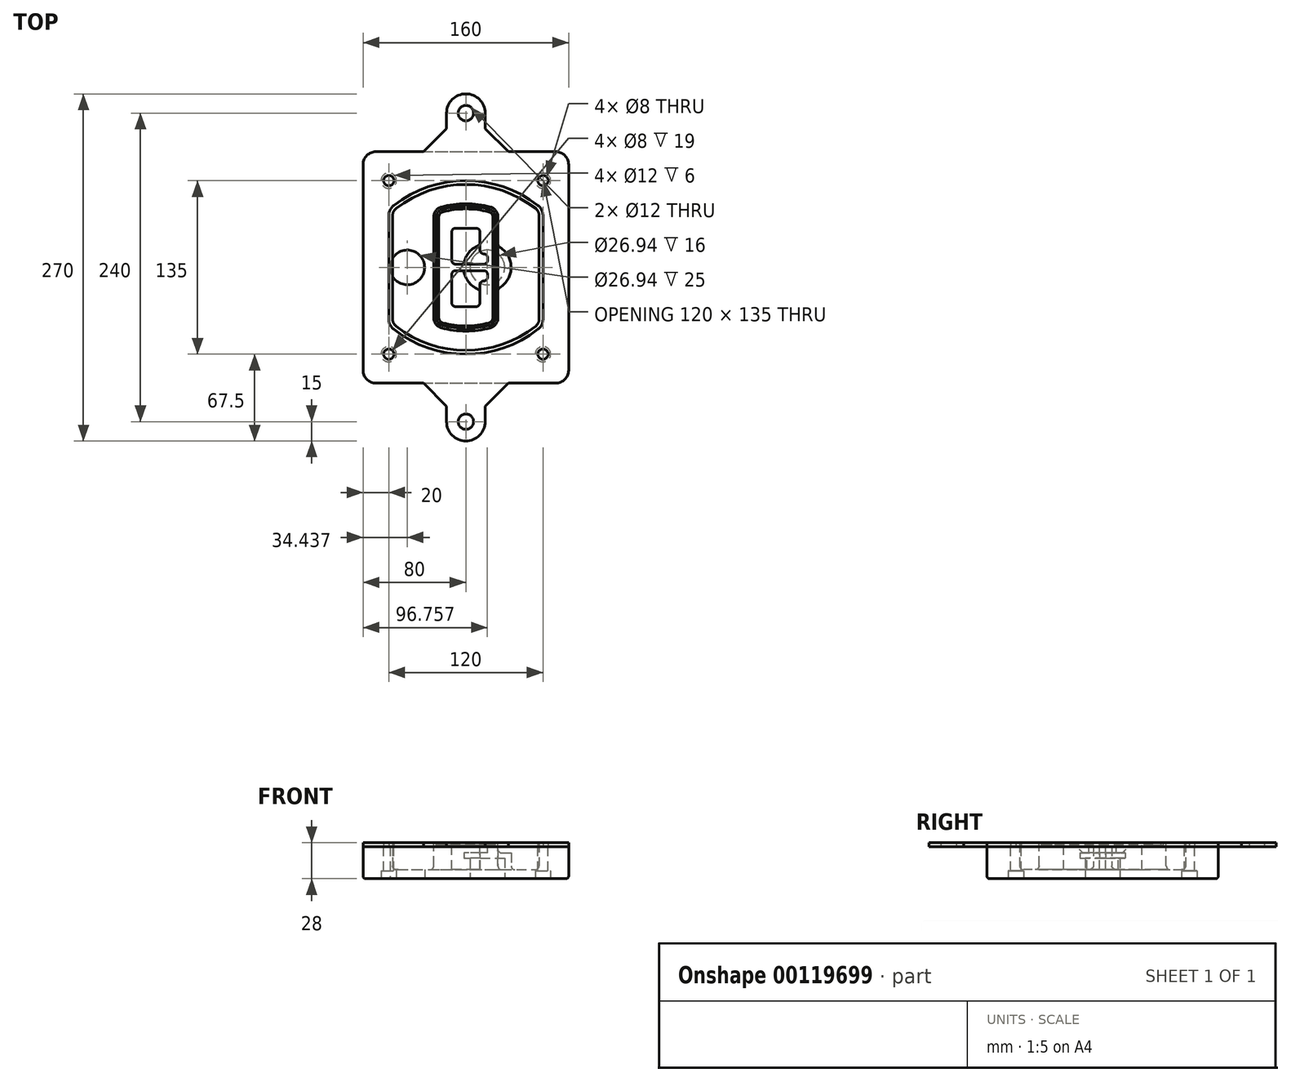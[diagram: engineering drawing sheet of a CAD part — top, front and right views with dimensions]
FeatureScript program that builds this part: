
annotation { "Feature Type Name" : "Feature", "Feature Type Description" : "" }
export const myFeature = defineFeature(function(context is Context, id is Id, definition is map)
    precondition{}
    {
        {
            var Q0;
            Q0=qCreatedBy(makeId("Top.planeOp"),FACE);
            var sketch = newSketch(context, id + "F0", { "sketchPlane" : qUnion([Q0])});
            skPoint(sketch, "E0.rect.middle", {"position": v(0, 0) * mm});
            skLineSegment(sketch, "E1.bottom", {"start": v(-70, -90) * mm, "end": v(70, -90) * mm});
            skLineSegment(sketch, "E1.top", {"start": v(-70, 90) * mm, "end": v(70, 90) * mm});
            skLineSegment(sketch, "E1.left", {"start": v(-80, -80) * mm, "end": v(-80, 80) * mm});
            skLineSegment(sketch, "E1.right", {"start": v(80, -80) * mm, "end": v(80, 80) * mm});
            skLineSegment(sketch, "E2", {"start": v(-80, 90) * mm, "end": v(80, -90) * mm, "construction": true});
            skLineSegment(sketch, "E3", {"start": v(80, 90) * mm, "end": v(-80, -90) * mm, "construction": true});
            skCircle(sketch, "E4", {"center": v(-60, 67.5) * mm, "radius": 4 * mm});
            skCircle(sketch, "E5", {"center": v(60, 67.5) * mm, "radius": 4 * mm});
            skCircle(sketch, "E6", {"center": v(60, -67.5) * mm, "radius": 4 * mm});
            skCircle(sketch, "E7", {"center": v(-60, -67.5) * mm, "radius": 4 * mm});
            skLineSegment(sketch, "E8", {"start": v(-60, 67.5) * mm, "end": v(60, 67.5) * mm, "construction": true});
            skLineSegment(sketch, "E9", {"start": v(60, 67.5) * mm, "end": v(60, -67.5) * mm, "construction": true});
            skLineSegment(sketch, "E10", {"start": v(60, -67.5) * mm, "end": v(-60, -67.5) * mm, "construction": true});
            skLineSegment(sketch, "E11", {"start": v(-60, -67.5) * mm, "end": v(-60, 67.5) * mm, "construction": true});
            skLineSegment(sketch, "E12", {"start": v(-60, 40.3) * mm, "end": v(-60, -40.3) * mm});
            skLineSegment(sketch, "E13", {"start": v(60, 40.3) * mm, "end": v(60, -40.3) * mm});
            skArc(sketch, "E14", {"start": v(56.15, 48.18) * mm, "mid": v(0, 67.5) * mm, "end": v(-56.15, 48.18) * mm});
            skArc(sketch, "E15", {"start": v(-56.15, -48.18) * mm, "mid": v(0, -67.5) * mm, "end": v(56.15, -48.18) * mm});
            skLineSegment(sketch, "E16", {"start": v(-60, 0) * mm, "end": v(60, 0) * mm, "construction": true});
            skPoint(sketch, "E17.visualSharp", {"position": v(-60, -45) * mm});
            skArc(sketch, "E17.filletArc", {"start": v(-60, -40.3) * mm, "mid": v(-58.99, -44.68) * mm, "end": v(-56.15, -48.18) * mm});
            skPoint(sketch, "E18.visualSharp", {"position": v(-60, 45) * mm});
            skArc(sketch, "E18.filletArc", {"start": v(-56.15, 48.18) * mm, "mid": v(-58.99, 44.68) * mm, "end": v(-60, 40.3) * mm});
            skPoint(sketch, "E19.visualSharp", {"position": v(60, 45) * mm});
            skArc(sketch, "E19.filletArc", {"start": v(60, 40.3) * mm, "mid": v(58.99, 44.68) * mm, "end": v(56.15, 48.18) * mm});
            skPoint(sketch, "E20.visualSharp", {"position": v(60, -45) * mm});
            skArc(sketch, "E20.filletArc", {"start": v(56.15, -48.18) * mm, "mid": v(58.99, -44.68) * mm, "end": v(60, -40.3) * mm});
            skPoint(sketch, "E21.visualSharp", {"position": v(-80, 90) * mm});
            skArc(sketch, "E21.filletArc", {"start": v(-70, 90) * mm, "mid": v(-77.07, 87.07) * mm, "end": v(-80, 80) * mm});
            skPoint(sketch, "E22.visualSharp", {"position": v(80, 90) * mm});
            skArc(sketch, "E22.filletArc", {"start": v(80, 80) * mm, "mid": v(77.07, 87.07) * mm, "end": v(70, 90) * mm});
            skPoint(sketch, "E23.visualSharp", {"position": v(80, -90) * mm});
            skArc(sketch, "E23.filletArc", {"start": v(70, -90) * mm, "mid": v(77.07, -87.07) * mm, "end": v(80, -80) * mm});
            skPoint(sketch, "E24.visualSharp", {"position": v(-80, -90) * mm});
            skArc(sketch, "E24.filletArc", {"start": v(-80, -80) * mm, "mid": v(-77.07, -87.07) * mm, "end": v(-70, -90) * mm});
            skArc(sketch, "E25.0", {"start": v(57, 40.3) * mm, "mid": v(56.3, 43.36) * mm, "end": v(54.3, 45.81) * mm});
            skLineSegment(sketch, "E25.1", {"start": v(57, 40.3) * mm, "end": v(57, -40.3) * mm});
            skArc(sketch, "E25.2", {"start": v(54.3, -45.81) * mm, "mid": v(56.3, -43.36) * mm, "end": v(57, -40.3) * mm});
            skArc(sketch, "E25.3", {"start": v(-54.3, -45.81) * mm, "mid": v(0, -64.5) * mm, "end": v(54.3, -45.81) * mm});
            skArc(sketch, "E25.4", {"start": v(-57, -40.3) * mm, "mid": v(-56.3, -43.36) * mm, "end": v(-54.3, -45.81) * mm});
            skArc(sketch, "E25.5", {"start": v(54.3, 45.81) * mm, "mid": v(0, 64.5) * mm, "end": v(-54.3, 45.81) * mm});
            skLineSegment(sketch, "E25.6", {"start": v(-57, 40.3) * mm, "end": v(-57, -40.3) * mm});
            skArc(sketch, "E25.7", {"start": v(-54.3, 45.81) * mm, "mid": v(-56.3, 43.36) * mm, "end": v(-57, 40.3) * mm});
            skArc(sketch, "E26.0", {"start": v(-58.62, 51.33) * mm, "mid": v(-62.58, 46.43) * mm, "end": v(-64, 40.3) * mm});
            skArc(sketch, "E26.1", {"start": v(58.62, 51.33) * mm, "mid": v(0, 71.5) * mm, "end": v(-58.62, 51.33) * mm});
            skArc(sketch, "E26.2", {"start": v(64, 40.3) * mm, "mid": v(62.58, 46.43) * mm, "end": v(58.62, 51.33) * mm});
            skLineSegment(sketch, "E26.3", {"start": v(64, 40.3) * mm, "end": v(64, -40.3) * mm});
            skArc(sketch, "E26.4", {"start": v(58.62, -51.33) * mm, "mid": v(62.58, -46.43) * mm, "end": v(64, -40.3) * mm});
            skLineSegment(sketch, "E26.5", {"start": v(-64, 40.3) * mm, "end": v(-64, -40.3) * mm});
            skArc(sketch, "E26.6", {"start": v(-58.62, -51.33) * mm, "mid": v(0, -71.5) * mm, "end": v(58.62, -51.33) * mm});
            skArc(sketch, "E26.7", {"start": v(-64, -40.3) * mm, "mid": v(-62.58, -46.43) * mm, "end": v(-58.62, -51.33) * mm});
            skSolve(sketch);
        }
        {
            var Q0;
            Q0=makeQuery(id+"F0.imprint","IMPRINT",FACE,{"disambiguationData":[TD([[makeQuery(id+"F0.imprint","IMPRINT",EDGE,{"derivedFrom":sQuery(id+"F0.wireOp",EDGE,"E1.bottom")}),1.0]])]});
            var Q1;
            Q1=makeQuery(id+"F0.imprint","IMPRINT",FACE,{"disambiguationData":[TD([[makeQuery(id+"F0.imprint","IMPRINT",EDGE,{"derivedFrom":sQuery(id+"F0.wireOp",EDGE,"E12")}),1.0]])]});
            var Q2;
            Q2=makeQuery(id+"F0.imprint","IMPRINT",FACE,{"disambiguationData":[TD([[makeQuery(id+"F0.imprint","IMPRINT",EDGE,{"derivedFrom":sQuery(id+"F0.wireOp",EDGE,"E25.0")}),1.0]])]});
            var Q3;
            Q3=makeQuery(id+"F0.imprint","IMPRINT",FACE,{"disambiguationData":[TD([[makeQuery(id+"F0.imprint","IMPRINT",EDGE,{"derivedFrom":sQuery(id+"F0.wireOp",EDGE,"E12")}),-1.0]])]});
            extrude(context, id + "F1", {"entities" : qUnion([Q0, Q1, Q2, Q3]), "oppositeDirection" : true, "depth" : 25 * mm});
        }
        {
            var Q0;
            Q0=makeQuery(id+"F0.imprint","IMPRINT",FACE,{"disambiguationData":[TD([[makeQuery(id+"F0.imprint","IMPRINT",EDGE,{"derivedFrom":sQuery(id+"F0.wireOp",EDGE,"E12")}),1.0]])]});
            extrude(context, id + "F2", {"entities" : qUnion([Q0]), "operationType" : NewBodyOperationType.ADD, "depth" : 3 * mm});
        }
        {
            var Q0;
            Q0=makeQuery(id+"F0.imprint","IMPRINT",FACE,{"disambiguationData":[TD([[makeQuery(id+"F0.imprint","IMPRINT",EDGE,{"derivedFrom":sQuery(id+"F0.wireOp",EDGE,"E25.0")}),1.0]])]});
            extrude(context, id + "F3", {"entities" : qUnion([Q0]), "operationType" : NewBodyOperationType.REMOVE, "oppositeDirection" : true, "depth" : 18 * mm});
        }
        {
            var Q0;
            Q0=makeQuery(id+"F2.opExtrude","CAP_FACE",FACE,{"disambiguationData":[OSD([sQuery(id+"F0.wireOp",EDGE,"E12"),sQuery(id+"F0.wireOp",EDGE,"E13"),sQuery(id+"F0.wireOp",EDGE,"E14"),sQuery(id+"F0.wireOp",EDGE,"E15"),sQuery(id+"F0.wireOp",EDGE,"E17.filletArc"),sQuery(id+"F0.wireOp",EDGE,"E18.filletArc"),sQuery(id+"F0.wireOp",EDGE,"E19.filletArc"),sQuery(id+"F0.wireOp",EDGE,"E20.filletArc"),sQuery(id+"F0.wireOp",EDGE,"E25.0"),sQuery(id+"F0.wireOp",EDGE,"E25.1"),sQuery(id+"F0.wireOp",EDGE,"E25.2"),sQuery(id+"F0.wireOp",EDGE,"E25.3"),sQuery(id+"F0.wireOp",EDGE,"E25.4"),sQuery(id+"F0.wireOp",EDGE,"E25.5"),sQuery(id+"F0.wireOp",EDGE,"E25.6"),sQuery(id+"F0.wireOp",EDGE,"E25.7")])],"isStart":false});
            var sketch = newSketch(context, id + "F4", { "sketchPlane" : qUnion([Q0])});
            skArc(sketch, "E27.0", {"start": v(-19.08, -46.97) * mm, "mid": v(0, -49.5) * mm, "end": v(19.08, -46.97) * mm});
            skArc(sketch, "E28.0", {"start": v(19.08, 46.97) * mm, "mid": v(0, 49.5) * mm, "end": v(-19.08, 46.97) * mm});
            skLineSegment(sketch, "E29", {"start": v(-25, 39.25) * mm, "end": v(-25, -39.25) * mm});
            skLineSegment(sketch, "E30", {"start": v(25, 39.25) * mm, "end": v(25, -39.25) * mm});
            skLineSegment(sketch, "E31", {"start": v(-25, 45.1) * mm, "end": v(25, 45.1) * mm, "construction": true});
            skLineSegment(sketch, "E32", {"start": v(-25, -45.1) * mm, "end": v(25, -45.1) * mm, "construction": true});
            skPoint(sketch, "E33.visualSharp", {"position": v(-25, 45.1) * mm});
            skArc(sketch, "E33.filletArc", {"start": v(-19.08, 46.97) * mm, "mid": v(-23.35, 44.11) * mm, "end": v(-25, 39.25) * mm});
            skPoint(sketch, "E34.visualSharp", {"position": v(25, 45.1) * mm});
            skArc(sketch, "E34.filletArc", {"start": v(25, 39.25) * mm, "mid": v(23.35, 44.11) * mm, "end": v(19.08, 46.97) * mm});
            skPoint(sketch, "E35.visualSharp", {"position": v(25, -45.1) * mm});
            skArc(sketch, "E35.filletArc", {"start": v(19.08, -46.97) * mm, "mid": v(23.35, -44.11) * mm, "end": v(25, -39.25) * mm});
            skPoint(sketch, "E36.visualSharp", {"position": v(-25, -45.1) * mm});
            skArc(sketch, "E36.filletArc", {"start": v(-25, -39.25) * mm, "mid": v(-23.35, -44.11) * mm, "end": v(-19.08, -46.97) * mm});
            skArc(sketch, "E37.0", {"start": v(54.3, 45.81) * mm, "mid": v(0, 64.5) * mm, "end": v(-54.3, 45.81) * mm});
            skArc(sketch, "E37.1", {"start": v(-54.3, 45.81) * mm, "mid": v(-56.3, 43.36) * mm, "end": v(-57, 40.3) * mm});
            skLineSegment(sketch, "E37.2", {"start": v(-57, 40.3) * mm, "end": v(-57, -40.3) * mm});
            skArc(sketch, "E37.3", {"start": v(-57, -40.3) * mm, "mid": v(-56.3, -43.36) * mm, "end": v(-54.3, -45.81) * mm});
            skArc(sketch, "E37.4", {"start": v(-54.3, -45.81) * mm, "mid": v(0, -64.5) * mm, "end": v(54.3, -45.81) * mm});
            skArc(sketch, "E37.5", {"start": v(54.3, -45.81) * mm, "mid": v(56.3, -43.36) * mm, "end": v(57, -40.3) * mm});
            skLineSegment(sketch, "E37.6", {"start": v(57, 40.3) * mm, "end": v(57, -40.3) * mm});
            skArc(sketch, "E37.7", {"start": v(57, 40.3) * mm, "mid": v(56.3, 43.36) * mm, "end": v(54.3, 45.81) * mm});
            skLineSegment(sketch, "E38.0", {"start": v(23, 39.25) * mm, "end": v(23, -39.25) * mm});
            skArc(sketch, "E38.1", {"start": v(18.56, -45.04) * mm, "mid": v(21.76, -42.9) * mm, "end": v(23, -39.25) * mm});
            skArc(sketch, "E38.2", {"start": v(-18.56, -45.04) * mm, "mid": v(0, -47.5) * mm, "end": v(18.56, -45.04) * mm});
            skArc(sketch, "E38.3", {"start": v(-23, -39.25) * mm, "mid": v(-21.76, -42.9) * mm, "end": v(-18.56, -45.04) * mm});
            skLineSegment(sketch, "E38.4", {"start": v(-23, 39.25) * mm, "end": v(-23, -39.25) * mm});
            skArc(sketch, "E38.5", {"start": v(23, 39.25) * mm, "mid": v(21.76, 42.9) * mm, "end": v(18.56, 45.04) * mm});
            skArc(sketch, "E38.6", {"start": v(-18.56, 45.04) * mm, "mid": v(-21.76, 42.9) * mm, "end": v(-23, 39.25) * mm});
            skArc(sketch, "E38.7", {"start": v(18.56, 45.04) * mm, "mid": v(0, 47.5) * mm, "end": v(-18.56, 45.04) * mm});
            skArc(sketch, "E39.0", {"start": v(21, 39.25) * mm, "mid": v(20.18, 41.68) * mm, "end": v(18.04, 43.1) * mm});
            skLineSegment(sketch, "E39.1", {"start": v(21, 39.25) * mm, "end": v(21, -39.25) * mm});
            skArc(sketch, "E39.2", {"start": v(18.04, -43.1) * mm, "mid": v(20.18, -41.68) * mm, "end": v(21, -39.25) * mm});
            skArc(sketch, "E39.3", {"start": v(-18.04, -43.1) * mm, "mid": v(0, -45.5) * mm, "end": v(18.04, -43.1) * mm});
            skArc(sketch, "E39.4", {"start": v(-21, -39.25) * mm, "mid": v(-20.18, -41.68) * mm, "end": v(-18.04, -43.1) * mm});
            skArc(sketch, "E39.5", {"start": v(18.04, 43.1) * mm, "mid": v(0, 45.5) * mm, "end": v(-18.04, 43.1) * mm});
            skLineSegment(sketch, "E39.6", {"start": v(-21, 39.25) * mm, "end": v(-21, -39.25) * mm});
            skArc(sketch, "E39.7", {"start": v(-18.04, 43.1) * mm, "mid": v(-20.18, 41.68) * mm, "end": v(-21, 39.25) * mm});
            skLineSegment(sketch, "E40", {"start": v(-25, 0) * mm, "end": v(25, 0) * mm, "construction": true});
            skLineSegment(sketch, "E41", {"start": v(-11, 5.5) * mm, "end": v(-11, 27.5) * mm});
            skLineSegment(sketch, "E42", {"start": v(-8, 30.5) * mm, "end": v(8, 30.5) * mm});
            skLineSegment(sketch, "E43", {"start": v(11, 27.5) * mm, "end": v(11, 13.5) * mm});
            skLineSegment(sketch, "E44", {"start": v(14, 10.5) * mm, "end": v(14, 10.5) * mm});
            skLineSegment(sketch, "E45", {"start": v(17, 7.5) * mm, "end": v(17, 5.5) * mm});
            skLineSegment(sketch, "E46", {"start": v(14, 2.5) * mm, "end": v(-8, 2.5) * mm});
            skPoint(sketch, "E47.visualSharp", {"position": v(-11, 30.5) * mm});
            skArc(sketch, "E47.filletArc", {"start": v(-8, 30.5) * mm, "mid": v(-10.12, 29.62) * mm, "end": v(-11, 27.5) * mm});
            skPoint(sketch, "E48.visualSharp", {"position": v(11, 30.5) * mm});
            skArc(sketch, "E48.filletArc", {"start": v(11, 27.5) * mm, "mid": v(10.12, 29.62) * mm, "end": v(8, 30.5) * mm});
            skPoint(sketch, "E49.visualSharp", {"position": v(11, 10.5) * mm});
            skArc(sketch, "E49.filletArc", {"start": v(11, 13.5) * mm, "mid": v(11.88, 11.38) * mm, "end": v(14, 10.5) * mm});
            skPoint(sketch, "E50.visualSharp", {"position": v(17, 10.5) * mm});
            skArc(sketch, "E50.filletArc", {"start": v(17, 7.5) * mm, "mid": v(16.12, 9.62) * mm, "end": v(14, 10.5) * mm});
            skPoint(sketch, "E51.visualSharp", {"position": v(17, 2.5) * mm});
            skArc(sketch, "E51.filletArc", {"start": v(14, 2.5) * mm, "mid": v(16.12, 3.38) * mm, "end": v(17, 5.5) * mm});
            skPoint(sketch, "E52.visualSharp", {"position": v(-11, 2.5) * mm});
            skArc(sketch, "E52.filletArc", {"start": v(-11, 5.5) * mm, "mid": v(-10.12, 3.38) * mm, "end": v(-8, 2.5) * mm});
            skLineSegment(sketch, "E53.0.MirrorCS", {"start": v(14, -2.5) * mm, "end": v(-8, -2.5) * mm});
            skArc(sketch, "E54.0.MirrorCS", {"start": v(-11, -5.5) * mm, "mid": v(-10.12, -3.38) * mm, "end": v(-8, -2.5) * mm});
            skLineSegment(sketch, "E55.0.MirrorCS", {"start": v(-11, -5.5) * mm, "end": v(-11, -27.5) * mm});
            skArc(sketch, "E56.0.MirrorCS", {"start": v(-8, -30.5) * mm, "mid": v(-10.12, -29.62) * mm, "end": v(-11, -27.5) * mm});
            skLineSegment(sketch, "E57.0.MirrorCS", {"start": v(-8, -30.5) * mm, "end": v(8, -30.5) * mm});
            skArc(sketch, "E58.0.MirrorCS", {"start": v(11, -27.5) * mm, "mid": v(10.12, -29.62) * mm, "end": v(8, -30.5) * mm});
            skLineSegment(sketch, "E59.0.MirrorCS", {"start": v(11, -27.5) * mm, "end": v(11, -13.5) * mm});
            skArc(sketch, "E60.0.MirrorCS", {"start": v(11, -13.5) * mm, "mid": v(11.88, -11.38) * mm, "end": v(14, -10.5) * mm});
            skArc(sketch, "E61.0.MirrorCS", {"start": v(17, -7.5) * mm, "mid": v(16.12, -9.62) * mm, "end": v(14, -10.5) * mm});
            skLineSegment(sketch, "E62.0.MirrorCS", {"start": v(17, -7.5) * mm, "end": v(17, -5.5) * mm});
            skArc(sketch, "E63.0.MirrorCS", {"start": v(14, -2.5) * mm, "mid": v(16.12, -3.38) * mm, "end": v(17, -5.5) * mm});
            skSolve(sketch);
        }
        {
            var Q0;
            Q0=makeQuery(id+"F4.imprint","IMPRINT",FACE,{"disambiguationData":[TD([[makeQuery(id+"F4.imprint","IMPRINT",EDGE,{"derivedFrom":sQuery(id+"F4.wireOp",EDGE,"E27.0")}),1.0]])]});
            var Q1;
            Q1=makeQuery(id+"F4.imprint","IMPRINT",FACE,{"disambiguationData":[TD([[makeQuery(id+"F4.imprint","IMPRINT",EDGE,{"derivedFrom":sQuery(id+"F4.wireOp",EDGE,"E38.0")}),-1.0]])]});
            var Q2;
            Q2=makeQuery(id+"F4.imprint","IMPRINT",FACE,{"disambiguationData":[TD([[makeQuery(id+"F4.imprint","IMPRINT",EDGE,{"derivedFrom":sQuery(id+"F4.wireOp",EDGE,"E39.0")}),1.0]])]});
            extrude(context, id + "F5", {"entities" : qUnion([Q0, Q1, Q2]), "operationType" : NewBodyOperationType.ADD, "endBound" : BoundingType.UP_TO_NEXT, "oppositeDirection" : true, "depth" : 25 * mm});
        }
        {
            var Q0;
            Q0=makeQuery(id+"F4.imprint","IMPRINT",FACE,{"disambiguationData":[TD([[makeQuery(id+"F4.imprint","IMPRINT",EDGE,{"derivedFrom":sQuery(id+"F4.wireOp",EDGE,"E38.0")}),-1.0]])]});
            extrude(context, id + "F6", {"entities" : qUnion([Q0]), "operationType" : NewBodyOperationType.REMOVE, "oppositeDirection" : true, "depth" : 2 * mm});
        }
        {
            var Q0;
            Q0=makeQuery(id+"F1.opExtrude","CAP_FACE",FACE,{"disambiguationData":[OSD([sQuery(id+"F0.wireOp",EDGE,"E1.bottom"),sQuery(id+"F0.wireOp",EDGE,"E1.top"),sQuery(id+"F0.wireOp",EDGE,"E1.left"),sQuery(id+"F0.wireOp",EDGE,"E1.right"),sQuery(id+"F0.wireOp",EDGE,"E4"),sQuery(id+"F0.wireOp",EDGE,"E5"),sQuery(id+"F0.wireOp",EDGE,"E6"),sQuery(id+"F0.wireOp",EDGE,"E7"),sQuery(id+"F0.wireOp",EDGE,"E21.filletArc"),sQuery(id+"F0.wireOp",EDGE,"E22.filletArc"),sQuery(id+"F0.wireOp",EDGE,"E23.filletArc"),sQuery(id+"F0.wireOp",EDGE,"E24.filletArc")])],"isStart":false});
            var sketch = newSketch(context, id + "F7", { "sketchPlane" : qUnion([Q0])});
            skCircle(sketch, "E64", {"center": v(16.76, 0) * mm, "radius": 13.47 * mm});
            skCircle(sketch, "E65", {"center": v(-45.56, 0) * mm, "radius": 13.47 * mm});
            skLineSegment(sketch, "E66", {"start": v(80, 0) * mm, "end": v(-80, 0) * mm});
            skCircle(sketch, "E67", {"center": v(16.76, 0) * mm, "radius": 18.47 * mm});
            skCircle(sketch, "E68", {"center": v(60, -67.5) * mm, "radius": 6 * mm});
            skCircle(sketch, "E69", {"center": v(-60, -67.5) * mm, "radius": 6 * mm});
            skCircle(sketch, "E70", {"center": v(-60, 67.5) * mm, "radius": 6 * mm});
            skCircle(sketch, "E71", {"center": v(60, 67.5) * mm, "radius": 6 * mm});
            skSolve(sketch);
        }
        {
            var Q0;
            {var subQ1=sQuery(id+"F7.wireOp",EDGE,"E66");var subQ4=sQuery(id+"F7.wireOp",EDGE,"E64");var subQ6=makeQuery(id+"F7.imprint","INTERSECT",VERTEX,{"disambiguationData":[OD(0.0)],"derivedFrom":[subQ4,subQ1]});Q0=makeQuery(id+"F7.imprint","IMPRINT",FACE,{"disambiguationData":[TD([[makeQuery(id+"F7.imprint","IMPRINT",EDGE,{"disambiguationData":[TD([[subQ6,-1.0]])],"derivedFrom":subQ4}),-1.0]])]});}
            var Q1;
            {var subQ0=sQuery(id+"F7.wireOp",EDGE,"E66");var subQ1=sQuery(id+"F7.wireOp",EDGE,"E64");var subQ3=makeQuery(id+"F7.imprint","INTERSECT",VERTEX,{"disambiguationData":[OD(0.0)],"derivedFrom":[subQ1,subQ0]});Q1=makeQuery(id+"F7.imprint","IMPRINT",FACE,{"disambiguationData":[TD([[makeQuery(id+"F7.imprint","IMPRINT",EDGE,{"disambiguationData":[TD([[subQ3,-1.0]])],"derivedFrom":subQ1}),1.0]])]});}
            var Q2;
            {var subQ0=sQuery(id+"F7.wireOp",EDGE,"E66");var subQ1=sQuery(id+"F7.wireOp",EDGE,"E64");var subQ3=makeQuery(id+"F7.imprint","INTERSECT",VERTEX,{"disambiguationData":[OD(0.0)],"derivedFrom":[subQ1,subQ0]});Q2=makeQuery(id+"F7.imprint","IMPRINT",FACE,{"disambiguationData":[TD([[makeQuery(id+"F7.imprint","IMPRINT",EDGE,{"disambiguationData":[TD([[subQ3,1.0]])],"derivedFrom":subQ1}),1.0]])]});}
            var Q3;
            {var subQ1=sQuery(id+"F7.wireOp",EDGE,"E66");var subQ4=sQuery(id+"F7.wireOp",EDGE,"E64");var subQ6=makeQuery(id+"F7.imprint","INTERSECT",VERTEX,{"disambiguationData":[OD(0.0)],"derivedFrom":[subQ4,subQ1]});Q3=makeQuery(id+"F7.imprint","IMPRINT",FACE,{"disambiguationData":[TD([[makeQuery(id+"F7.imprint","IMPRINT",EDGE,{"disambiguationData":[TD([[subQ6,1.0]])],"derivedFrom":subQ4}),-1.0]])]});}
            extrude(context, id + "F8", {"entities" : qUnion([Q0, Q1, Q2, Q3]), "operationType" : NewBodyOperationType.ADD, "oppositeDirection" : true, "depth" : 20 * mm});
        }
        {
            var Q0;
            {var subQ0=sQuery(id+"F7.wireOp",EDGE,"E66");var subQ1=sQuery(id+"F7.wireOp",EDGE,"E64");var subQ3=makeQuery(id+"F7.imprint","INTERSECT",VERTEX,{"disambiguationData":[OD(0.0)],"derivedFrom":[subQ1,subQ0]});Q0=makeQuery(id+"F7.imprint","IMPRINT",FACE,{"disambiguationData":[TD([[makeQuery(id+"F7.imprint","IMPRINT",EDGE,{"disambiguationData":[TD([[subQ3,-1.0]])],"derivedFrom":subQ1}),1.0]])]});}
            var Q1;
            {var subQ0=sQuery(id+"F7.wireOp",EDGE,"E66");var subQ1=sQuery(id+"F7.wireOp",EDGE,"E64");var subQ3=makeQuery(id+"F7.imprint","INTERSECT",VERTEX,{"disambiguationData":[OD(0.0)],"derivedFrom":[subQ1,subQ0]});Q1=makeQuery(id+"F7.imprint","IMPRINT",FACE,{"disambiguationData":[TD([[makeQuery(id+"F7.imprint","IMPRINT",EDGE,{"disambiguationData":[TD([[subQ3,1.0]])],"derivedFrom":subQ1}),1.0]])]});}
            extrude(context, id + "F9", {"entities" : qUnion([Q0, Q1]), "operationType" : NewBodyOperationType.REMOVE, "oppositeDirection" : true, "depth" : 16 * mm});
        }
        {
            var Q0;
            {var subQ0=sQuery(id+"F7.wireOp",EDGE,"E66");var subQ1=sQuery(id+"F7.wireOp",EDGE,"E65");var subQ3=makeQuery(id+"F7.imprint","INTERSECT",VERTEX,{"disambiguationData":[OD(0.0)],"derivedFrom":[subQ1,subQ0]});Q0=makeQuery(id+"F7.imprint","IMPRINT",FACE,{"disambiguationData":[TD([[makeQuery(id+"F7.imprint","IMPRINT",EDGE,{"disambiguationData":[TD([[subQ3,-1.0]])],"derivedFrom":subQ1}),1.0]])]});}
            var Q1;
            {var subQ0=sQuery(id+"F7.wireOp",EDGE,"E66");var subQ1=sQuery(id+"F7.wireOp",EDGE,"E65");var subQ3=makeQuery(id+"F7.imprint","INTERSECT",VERTEX,{"disambiguationData":[OD(0.0)],"derivedFrom":[subQ1,subQ0]});Q1=makeQuery(id+"F7.imprint","IMPRINT",FACE,{"disambiguationData":[TD([[makeQuery(id+"F7.imprint","IMPRINT",EDGE,{"disambiguationData":[TD([[subQ3,1.0]])],"derivedFrom":subQ1}),1.0]])]});}
            extrude(context, id + "F10", {"entities" : qUnion([Q0, Q1]), "operationType" : NewBodyOperationType.REMOVE, "oppositeDirection" : true, "depth" : 25 * mm});
        }
        {
            var Q0;
            Q0=makeQuery(id+"F7.imprint","IMPRINT",FACE,{"disambiguationData":[TD([[makeQuery(id+"F7.imprint","IMPRINT",EDGE,{"derivedFrom":sQuery(id+"F7.wireOp",EDGE,"E68")}),1.0]])]});
            var Q1;
            Q1=makeQuery(id+"F7.imprint","IMPRINT",FACE,{"disambiguationData":[TD([[makeQuery(id+"F7.imprint","IMPRINT",EDGE,{"derivedFrom":makeQuery(id+"F1.opExtrude","CAP_EDGE",EDGE,{"disambiguationData":[OSD([sQuery(id+"F0.wireOp",EDGE,"E5")])],"isStart":false})}),-1.0]])]});
            var Q2;
            Q2=makeQuery(id+"F7.imprint","IMPRINT",FACE,{"disambiguationData":[TD([[makeQuery(id+"F7.imprint","IMPRINT",EDGE,{"derivedFrom":sQuery(id+"F7.wireOp",EDGE,"E69")}),1.0]])]});
            var Q3;
            Q3=makeQuery(id+"F7.imprint","IMPRINT",FACE,{"disambiguationData":[TD([[makeQuery(id+"F7.imprint","IMPRINT",EDGE,{"derivedFrom":makeQuery(id+"F1.opExtrude","CAP_EDGE",EDGE,{"disambiguationData":[OSD([sQuery(id+"F0.wireOp",EDGE,"E4")])],"isStart":false})}),-1.0]])]});
            var Q4;
            Q4=makeQuery(id+"F7.imprint","IMPRINT",FACE,{"disambiguationData":[TD([[makeQuery(id+"F7.imprint","IMPRINT",EDGE,{"derivedFrom":sQuery(id+"F7.wireOp",EDGE,"E70")}),1.0]])]});
            var Q5;
            Q5=makeQuery(id+"F7.imprint","IMPRINT",FACE,{"disambiguationData":[TD([[makeQuery(id+"F7.imprint","IMPRINT",EDGE,{"derivedFrom":makeQuery(id+"F1.opExtrude","CAP_EDGE",EDGE,{"disambiguationData":[OSD([sQuery(id+"F0.wireOp",EDGE,"E7")])],"isStart":false})}),-1.0]])]});
            var Q6;
            Q6=makeQuery(id+"F7.imprint","IMPRINT",FACE,{"disambiguationData":[TD([[makeQuery(id+"F7.imprint","IMPRINT",EDGE,{"derivedFrom":sQuery(id+"F7.wireOp",EDGE,"E71")}),1.0]])]});
            var Q7;
            Q7=makeQuery(id+"F7.imprint","IMPRINT",FACE,{"disambiguationData":[TD([[makeQuery(id+"F7.imprint","IMPRINT",EDGE,{"derivedFrom":makeQuery(id+"F1.opExtrude","CAP_EDGE",EDGE,{"disambiguationData":[OSD([sQuery(id+"F0.wireOp",EDGE,"E6")])],"isStart":false})}),-1.0]])]});
            extrude(context, id + "F11", {"entities" : qUnion([Q0, Q1, Q2, Q3, Q4, Q5, Q6, Q7]), "operationType" : NewBodyOperationType.REMOVE, "oppositeDirection" : true, "depth" : 6 * mm});
        }
        {
            var Q0;
            Q0=makeQuery(id+"F9.boolean.opBoolean","COPY",FACE,{"derivedFrom":makeQuery(id+"F9.opExtrude","CAP_FACE",FACE,{"disambiguationData":[OSD([sQuery(id+"F7.wireOp",EDGE,"E64")])],"isStart":false})});
            var sketch = newSketch(context, id + "F12", { "sketchPlane" : qUnion([Q0])});
            skArc(sketch, "E72.0", {"start": v(11, 17.55) * mm, "mid": v(2.57, 11.82) * mm, "end": v(-1.54, 2.5) * mm});
            skArc(sketch, "E72.1", {"start": v(-1.54, -2.5) * mm, "mid": v(2.57, -11.82) * mm, "end": v(11, -17.55) * mm});
            skLineSegment(sketch, "E73", {"start": v(-1.54, -2.5) * mm, "end": v(14, -2.5) * mm});
            skLineSegment(sketch, "E74.0", {"start": v(14, 2.5) * mm, "end": v(-1.54, 2.5) * mm});
            skArc(sketch, "E74.1", {"start": v(14, 2.5) * mm, "mid": v(16.12, 3.38) * mm, "end": v(17, 5.5) * mm});
            skLineSegment(sketch, "E74.2", {"start": v(17, 7.5) * mm, "end": v(17, 5.5) * mm});
            skArc(sketch, "E74.3", {"start": v(17, 7.5) * mm, "mid": v(16.12, 9.62) * mm, "end": v(14, 10.5) * mm});
            skArc(sketch, "E74.4", {"start": v(11, 13.5) * mm, "mid": v(11.88, 11.38) * mm, "end": v(14, 10.5) * mm});
            skLineSegment(sketch, "E74.5", {"start": v(11, 17.55) * mm, "end": v(11, 13.5) * mm});
            skLineSegment(sketch, "E74.7", {"start": v(14, -2.5) * mm, "end": v(-1.54, -2.5) * mm});
            skArc(sketch, "E74.8", {"start": v(14, -2.5) * mm, "mid": v(16.12, -3.38) * mm, "end": v(17, -5.5) * mm});
            skLineSegment(sketch, "E74.9", {"start": v(17, -7.5) * mm, "end": v(17, -5.5) * mm});
            skArc(sketch, "E74.10", {"start": v(17, -7.5) * mm, "mid": v(16.12, -9.62) * mm, "end": v(14, -10.5) * mm});
            skArc(sketch, "E74.11", {"start": v(11, -13.5) * mm, "mid": v(11.88, -11.38) * mm, "end": v(14, -10.5) * mm});
            skLineSegment(sketch, "E74.12", {"start": v(11, -17.55) * mm, "end": v(11, -13.5) * mm});
            skPoint(sketch, "E75.orphan", {"position": v(11, -27.5) * mm});
            skPoint(sketch, "E76.orphan", {"position": v(-8, -2.5) * mm});
            skPoint(sketch, "E77.orphan", {"position": v(-8, 2.5) * mm});
            skPoint(sketch, "E78.orphan", {"position": v(11, 27.5) * mm});
            skSolve(sketch);
        }
        {
            var Q0;
            {var subQ7=sQuery(id+"F12.wireOp",EDGE,"E72.0");var subQ14=sQuery(id+"F12.wireOp",EDGE,"E72.1");var subQ16=sQuery(id+"F12.wireOp",EDGE,"E74.1");var subQ18=sQuery(id+"F12.wireOp",EDGE,"E74.8");Q0=qUnion([makeQuery(id+"F12.imprint","IMPRINT",FACE,{"disambiguationData":[TD([[makeQuery(id+"F12.imprint","IMPRINT",EDGE,{"derivedFrom":subQ7}),1.0]])]}),makeQuery(id+"F12.imprint","IMPRINT",FACE,{"disambiguationData":[TD([[makeQuery(id+"F12.imprint","IMPRINT",EDGE,{"derivedFrom":subQ14}),1.0]])]}),makeQuery(id+"F12.imprint","IMPRINT",FACE,{"disambiguationData":[TD([[makeQuery(id+"F12.imprint","IMPRINT",EDGE,{"derivedFrom":subQ16}),1.0]])]}),makeQuery(id+"F12.imprint","IMPRINT",FACE,{"disambiguationData":[TD([[makeQuery(id+"F12.imprint","IMPRINT",EDGE,{"derivedFrom":subQ18}),-1.0]])]})]);}
            var Q1;
            Q1=makeQuery(id+"F5.boolean.opBoolean","SPLIT",FACE,{"disambiguationData":[TD([makeQuery(id+"F5.opExtrude","SWEPT_FACE",FACE,{"disambiguationData":[OSD([sQuery(id+"F4.wireOp",EDGE,"E41")])]})])],"derivedFrom":makeQuery(id+"F3.boolean.opBoolean","COPY",FACE,{"derivedFrom":makeQuery(id+"F3.opExtrude","CAP_FACE",FACE,{"disambiguationData":[OSD([sQuery(id+"F0.wireOp",EDGE,"E25.0"),sQuery(id+"F0.wireOp",EDGE,"E25.1"),sQuery(id+"F0.wireOp",EDGE,"E25.2"),sQuery(id+"F0.wireOp",EDGE,"E25.3"),sQuery(id+"F0.wireOp",EDGE,"E25.4"),sQuery(id+"F0.wireOp",EDGE,"E25.5"),sQuery(id+"F0.wireOp",EDGE,"E25.6"),sQuery(id+"F0.wireOp",EDGE,"E25.7")])],"isStart":false})})});
            extrude(context, id + "F13", {"entities" : qUnion([Q0]), "operationType" : NewBodyOperationType.REMOVE, "endBound" : BoundingType.UP_TO_SURFACE, "endBoundEntityFace" : qUnion([Q1]), "depth" : 25 * mm});
        }
        {
            var Q0;
            Q0=makeQuery(id+"F3.boolean.opBoolean","COPY",EDGE,{"derivedFrom":makeQuery(id+"F3.opExtrude","CAP_EDGE",EDGE,{"disambiguationData":[OSD([sQuery(id+"F0.wireOp",EDGE,"E25.6")])],"isStart":false})});
            var Q1;
            Q1=makeQuery(id+"F8.boolean.opBoolean","INTERSECT",EDGE,{"derivedFrom":[makeQuery(id+"F5.opExtrude","SWEPT_FACE",FACE,{"disambiguationData":[OSD([sQuery(id+"F4.wireOp",EDGE,"E30")])]}),makeQuery(id+"F8.opExtrude","CAP_FACE",FACE,{"disambiguationData":[OSD([sQuery(id+"F7.wireOp",EDGE,"E67")])],"isStart":false})]});
            var Q2;
            Q2=makeQuery(id+"F8.boolean.opBoolean","INTERSECT",EDGE,{"disambiguationData":[OD(1.0)],"derivedFrom":[makeQuery(id+"F5.opExtrude","SWEPT_FACE",FACE,{"disambiguationData":[OSD([sQuery(id+"F4.wireOp",EDGE,"E30")])]}),makeQuery(id+"F8.opExtrude","SWEPT_FACE",FACE,{"disambiguationData":[OSD([sQuery(id+"F7.wireOp",EDGE,"E67")])]})]});
            var Q3;
            {var subQ0=sQuery(id+"F4.wireOp",EDGE,"E30");Q3=makeQuery(id+"F8.boolean.opBoolean","SPLIT",EDGE,{"disambiguationData":[TD([makeQuery(id+"F5.opExtrude","SWEPT_FACE",FACE,{"disambiguationData":[OSD([sQuery(id+"F4.wireOp",EDGE,"E35.filletArc")])]})])],"derivedFrom":makeQuery(id+"F5.opExtrude","CAP_EDGE",EDGE,{"disambiguationData":[OSD([subQ0])],"isStart":false})});}
            var Q4;
            {var subQ0=sQuery(id+"F0.wireOp",EDGE,"E25.7");var subQ1=sQuery(id+"F0.wireOp",EDGE,"E25.1");var subQ2=sQuery(id+"F0.wireOp",EDGE,"E25.6");var subQ3=sQuery(id+"F0.wireOp",EDGE,"E25.5");var subQ4=sQuery(id+"F0.wireOp",EDGE,"E25.4");var subQ5=sQuery(id+"F0.wireOp",EDGE,"E25.0");var subQ6=sQuery(id+"F0.wireOp",EDGE,"E25.2");var subQ7=sQuery(id+"F0.wireOp",EDGE,"E25.3");Q4=makeQuery(id+"F8.boolean.opBoolean","INTERSECT",EDGE,{"derivedFrom":[makeQuery(id+"F5.boolean.opBoolean","SPLIT",FACE,{"disambiguationData":[TD([makeQuery(id+"F2.opExtrude","SWEPT_FACE",FACE,{"disambiguationData":[OSD([subQ5])]})])],"derivedFrom":makeQuery(id+"F3.boolean.opBoolean","COPY",FACE,{"derivedFrom":makeQuery(id+"F3.opExtrude","CAP_FACE",FACE,{"disambiguationData":[OSD([subQ5,subQ1,subQ6,subQ7,subQ4,subQ3,subQ2,subQ0])],"isStart":false})})}),makeQuery(id+"F8.opExtrude","SWEPT_FACE",FACE,{"disambiguationData":[OSD([sQuery(id+"F7.wireOp",EDGE,"E67")])]})]});}
            var Q5;
            Q5=makeQuery(id+"F8.boolean.opBoolean","INTERSECT",EDGE,{"disambiguationData":[OD(0.0)],"derivedFrom":[makeQuery(id+"F5.opExtrude","SWEPT_FACE",FACE,{"disambiguationData":[OSD([sQuery(id+"F4.wireOp",EDGE,"E30")])]}),makeQuery(id+"F8.opExtrude","SWEPT_FACE",FACE,{"disambiguationData":[OSD([sQuery(id+"F7.wireOp",EDGE,"E67")])]})]});
            fillet(context, id + "F14", {"entities" : qUnion([Q0, Q1, Q2, Q3, Q4, Q5]), "radius" : 3 * mm, "tangentPropagation" : true, "allowEdgeOverflow" : false});
        }
        {
            var Q0;
            Q0=makeQuery(id+"F1.opExtrude","CAP_EDGE",EDGE,{"disambiguationData":[OSD([sQuery(id+"F0.wireOp",EDGE,"E1.bottom")])],"isStart":false});
            fillet(context, id + "F15", {"entities" : qUnion([Q0]), "radius" : 2 * mm, "tangentPropagation" : true, "allowEdgeOverflow" : false});
        }
        {
            var Q0;
            {var subQ0=sQuery(id+"F0.wireOp",EDGE,"E22.filletArc");var subQ1=sQuery(id+"F0.wireOp",EDGE,"E7");var subQ2=sQuery(id+"F0.wireOp",EDGE,"E6");var subQ3=sQuery(id+"F0.wireOp",EDGE,"E5");var subQ4=sQuery(id+"F0.wireOp",EDGE,"E4");var subQ5=sQuery(id+"F0.wireOp",EDGE,"E1.bottom");var subQ6=sQuery(id+"F0.wireOp",EDGE,"E21.filletArc");var subQ7=sQuery(id+"F0.wireOp",EDGE,"E1.top");var subQ8=sQuery(id+"F0.wireOp",EDGE,"E1.left");var subQ9=sQuery(id+"F0.wireOp",EDGE,"E1.right");var subQ10=sQuery(id+"F0.wireOp",EDGE,"E23.filletArc");var subQ11=sQuery(id+"F0.wireOp",EDGE,"E24.filletArc");Q0=makeQuery(id+"F2.boolean.opBoolean","SPLIT",FACE,{"disambiguationData":[TD([makeQuery(id+"F1.opExtrude","SWEPT_FACE",FACE,{"disambiguationData":[OSD([subQ5])]})])],"derivedFrom":makeQuery(id+"F1.opExtrude","CAP_FACE",FACE,{"disambiguationData":[OSD([subQ5,subQ7,subQ8,subQ9,subQ4,subQ3,subQ2,subQ1,subQ6,subQ0,subQ10,subQ11])],"isStart":true})});}
            var sketch = newSketch(context, id + "F16", { "sketchPlane" : qUnion([Q0])});
            skLineSegment(sketch, "E79.0", {"start": v(-70, 90) * mm, "end": v(70, 90) * mm});
            skArc(sketch, "E79.1", {"start": v(-70, 90) * mm, "mid": v(-77.07, 87.07) * mm, "end": v(-80, 80) * mm});
            skLineSegment(sketch, "E79.2", {"start": v(-80, -80) * mm, "end": v(-80, 80) * mm});
            skArc(sketch, "E79.3", {"start": v(-80, -80) * mm, "mid": v(-77.07, -87.07) * mm, "end": v(-70, -90) * mm});
            skLineSegment(sketch, "E79.4", {"start": v(-70, -90) * mm, "end": v(70, -90) * mm});
            skArc(sketch, "E79.5", {"start": v(70, -90) * mm, "mid": v(77.07, -87.07) * mm, "end": v(80, -80) * mm});
            skLineSegment(sketch, "E79.6", {"start": v(80, -80) * mm, "end": v(80, 80) * mm});
            skArc(sketch, "E79.7", {"start": v(80, 80) * mm, "mid": v(77.07, 87.07) * mm, "end": v(70, 90) * mm});
            skArc(sketch, "E79.8", {"start": v(56.15, 48.18) * mm, "mid": v(0, 67.5) * mm, "end": v(-56.15, 48.18) * mm});
            skArc(sketch, "E79.9", {"start": v(60, 40.3) * mm, "mid": v(58.99, 44.68) * mm, "end": v(56.15, 48.18) * mm});
            skLineSegment(sketch, "E79.10", {"start": v(60, 40.3) * mm, "end": v(60, -40.3) * mm});
            skArc(sketch, "E79.11", {"start": v(56.15, -48.18) * mm, "mid": v(58.99, -44.68) * mm, "end": v(60, -40.3) * mm});
            skArc(sketch, "E79.12", {"start": v(-56.15, -48.18) * mm, "mid": v(0, -67.5) * mm, "end": v(56.15, -48.18) * mm});
            skArc(sketch, "E79.13", {"start": v(-60, -40.3) * mm, "mid": v(-58.99, -44.68) * mm, "end": v(-56.15, -48.18) * mm});
            skLineSegment(sketch, "E79.14", {"start": v(-60, 40.3) * mm, "end": v(-60, -40.3) * mm});
            skArc(sketch, "E79.15", {"start": v(-56.15, 48.18) * mm, "mid": v(-58.99, 44.68) * mm, "end": v(-60, 40.3) * mm});
            skLineSegment(sketch, "E80", {"start": v(-33, 90) * mm, "end": v(-15, 108) * mm});
            skLineSegment(sketch, "E81", {"start": v(-15, 108) * mm, "end": v(-15, 120) * mm});
            skArc(sketch, "E82", {"start": v(15, 120) * mm, "mid": v(0, 135) * mm, "end": v(-15, 120) * mm});
            skLineSegment(sketch, "E83", {"start": v(15, 120) * mm, "end": v(15, 108) * mm});
            skLineSegment(sketch, "E84", {"start": v(15, 108) * mm, "end": v(33, 90) * mm});
            skLineSegment(sketch, "E85", {"start": v(0, 120) * mm, "end": v(0, 90) * mm, "construction": true});
            skCircle(sketch, "E86", {"center": v(0, 120) * mm, "radius": 6 * mm});
            skLineSegment(sketch, "E87", {"start": v(-80, 0) * mm, "end": v(80, 0) * mm, "construction": true});
            skLineSegment(sketch, "E88.MirrorCS", {"start": v(33, 90) * mm, "end": v(15, 108) * mm});
            skLineSegment(sketch, "E89.MirrorCS", {"start": v(-15, 108) * mm, "end": v(-33, 90) * mm});
            skArc(sketch, "E90.MirrorCS", {"start": v(-15, 120) * mm, "mid": v(0, 135) * mm, "end": v(15, 120) * mm});
            skLineSegment(sketch, "E91.MirrorCS", {"start": v(-15, 120) * mm, "end": v(-15, 108) * mm});
            skLineSegment(sketch, "E92.MirrorCS", {"start": v(15, 108) * mm, "end": v(15, 120) * mm});
            skLineSegment(sketch, "E93.MirrorCS", {"start": v(-15, -108) * mm, "end": v(-33, -90) * mm});
            skLineSegment(sketch, "E94.MirrorCS", {"start": v(-15, -120) * mm, "end": v(-15, -108) * mm});
            skArc(sketch, "E95.MirrorCS", {"start": v(15, -120) * mm, "mid": v(0, -135) * mm, "end": v(-15, -120) * mm});
            skLineSegment(sketch, "E96.MirrorCS", {"start": v(15, -120) * mm, "end": v(15, -108) * mm});
            skLineSegment(sketch, "E97.MirrorCS", {"start": v(33, -90) * mm, "end": v(15, -108) * mm});
            skLineSegment(sketch, "E98.MirrorCS", {"start": v(0, -120) * mm, "end": v(0, -90) * mm, "construction": true});
            skCircle(sketch, "E99.MirrorC", {"center": v(0, -120) * mm, "radius": 6 * mm});
            skCircle(sketch, "E100.0", {"center": v(-60, -67.5) * mm, "radius": 4 * mm});
            skCircle(sketch, "E100.1", {"center": v(-60, 67.5) * mm, "radius": 4 * mm});
            skCircle(sketch, "E100.2", {"center": v(60, 67.5) * mm, "radius": 4 * mm});
            skCircle(sketch, "E100.3", {"center": v(60, -67.5) * mm, "radius": 4 * mm});
            skSolve(sketch);
        }
        {
            var Q0;
            Q0 = qSketchRegion(id + "F16", true);
            var Q1;
            Q1=makeQuery(id+"F2.opExtrude","CAP_FACE",FACE,{"disambiguationData":[OSD([sQuery(id+"F0.wireOp",EDGE,"E12"),sQuery(id+"F0.wireOp",EDGE,"E13"),sQuery(id+"F0.wireOp",EDGE,"E14"),sQuery(id+"F0.wireOp",EDGE,"E15"),sQuery(id+"F0.wireOp",EDGE,"E17.filletArc"),sQuery(id+"F0.wireOp",EDGE,"E18.filletArc"),sQuery(id+"F0.wireOp",EDGE,"E19.filletArc"),sQuery(id+"F0.wireOp",EDGE,"E20.filletArc"),sQuery(id+"F0.wireOp",EDGE,"E25.0"),sQuery(id+"F0.wireOp",EDGE,"E25.1"),sQuery(id+"F0.wireOp",EDGE,"E25.2"),sQuery(id+"F0.wireOp",EDGE,"E25.3"),sQuery(id+"F0.wireOp",EDGE,"E25.4"),sQuery(id+"F0.wireOp",EDGE,"E25.5"),sQuery(id+"F0.wireOp",EDGE,"E25.6"),sQuery(id+"F0.wireOp",EDGE,"E25.7")])],"isStart":false});
            extrude(context, id + "F17", {"entities" : qUnion([Q0]), "endBound" : BoundingType.UP_TO_SURFACE, "endBoundEntityFace" : qUnion([Q1]), "depth" : 25 * mm});
        }
    });
